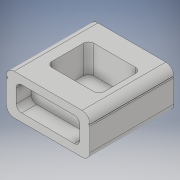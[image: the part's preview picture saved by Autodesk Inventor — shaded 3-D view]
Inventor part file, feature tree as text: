
AUTODESK INVENTOR PART (.ipt)
format: ipt  version: 2017 (Build 210142000, 142)  size: 181,248 bytes
history: native  units: in
note: dims shown in document units (in); Inventor stores cm internally (conversion verified against a paired STEP export)
features: extrude x6, sketch x6
ambient origin geometry x8: Origin, YZ Plane, XZ Plane, XY Plane, X Axis, Y Axis, Z Axis, Center Point
bodies: Solid1 (feature_tree)
feature tree (12):
  extrude  "Extrusion1"  Depth=1.53in
  extrude  "Extrusion2"  Depth=0.3in
  extrude  "Extrusion3"  Depth=0.3in
  extrude  "Extrusion4"  Depth=2.4in
  extrude  "Extrusion5"  Depth=0.2in
  extrude  "Extrusion6"  Depth=1.59in
  sketch  "Sketch1"  dims[d2=3.17in d3=1.53in]
  sketch  "Sketch2"  dims[d4=0.3in d5=0.3in]
  sketch  "Sketch3"  dims[d6=0.3in d7=0.3in]
  sketch  "Sketch4"  dims[d10=3.17in d11=0.0in d12=2.4in]
  sketch  "Sketch5"  dims[d13=0.93in d16=0.2in]
  sketch  "Sketch6"  dims[d17=0.57in d18=0.0in d19=1.59in d20=1.98in d21=0.5in d22=1.07in d23=0.0in d26=1.0in d27=2.5in d29=1.0in d30=0.2in d31=0.57in d32=0.0in d33=0.2in d34=0.06in d35=0.05in d36=0.0in d37=0.05in d38=0.0in]
